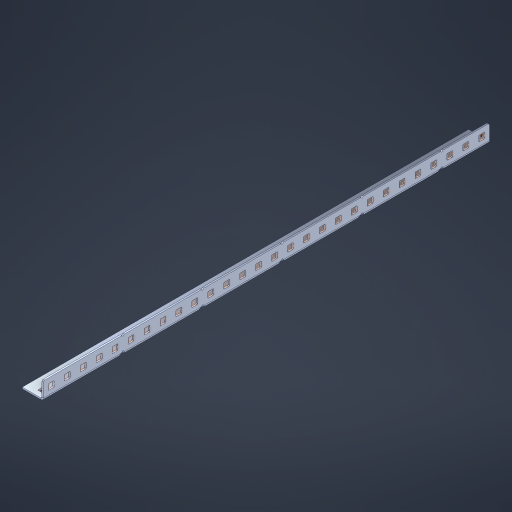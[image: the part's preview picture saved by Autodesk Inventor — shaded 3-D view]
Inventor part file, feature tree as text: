
AUTODESK INVENTOR PART (.ipt)
format: ipt  version: 2023 (Build 270158000, 158)  size: 908,288 bytes
history: native  units: in
note: dims shown in document units (in); Inventor stores cm internally (conversion verified against a paired STEP export)
features: other x61, extrude x55, sheet_metal_op x10, sketch x8, mirror x1, pattern_linear x1, chamfer x1
ambient origin geometry x8: Origin, YZ Plane, XZ Plane, XY Plane, X Axis, Y Axis, Z Axis, Center Point
bodies: Solid1 (feature_tree), Body (feature_tree)
feature tree (137):
  other  "Flange Pattern Plane"
  sheet_metal_op  "Flange Pattern"
  sheet_metal_op  "Body Pattern"
  other  "Arc Length"
  mirror  "Notch Mirror"
  pattern_linear  "Notch Pattern"  Spacing1=0.1875in  [1 undecoded]
  chamfer  "End Chamfer"
  extrude  "Half Cut"  Depth=0.0469in
  sketch  "Sketch1"  dims[d0=2.5in]
  other  "Plate1"
  sketch  "Sketch2"  dims[d1=14.0in]
  other  "Plate2"
  sheet_metal_op  "Bend1"
  sheet_metal_op  "Corner1"
  sketch  "Sketch3"  dims[d2=0.0469in]
  other  "Flange Pattern Sketch"
  sketch  "Sketch7"  dims[d3=0.0469in]
  other  "Srf1"
  other  "Srf2"
  sketch  "Sketch8"  dims[d4=0.0234in]
  sketch  "Sketch9"  dims[d5=0.0938in]
  other  "Srf91"
  sheet_metal_op  "Body Pattern Sketch"
  other  "Srf92"
  sketch  "Sketch13"  dims[d6=0.0469in]
  sketch  "Sketch14"  dims[d7=0.5in d8=90.0deg d9=0.0312in d10=0.1875in d11=0.0469in d12=0.0469in d16=0.182in d17=0.02in d18=0.0469in d19=0.0in d20=0.25in d21=0.25in d46=0.172in d47=1.0in d48=0.0in d49=0.182in d50=0.02in d51=0.25in d52=0.25in d53=0.0469in d54=0.0in d55=0.172in d56=1.0in d57=0.0in d60=11.0236in d62=0.5in d63=0.3937in d65=0.5in d85=0.1227in d86=0.1659in d88=0.04in d89=0.0469in d90=0.0in d91=0.04in d92=0.0491in d95=2.5in d96=0.04in d97=0.25in d98=45.0deg d101=0.0in d102=2.497in d131=0.5in d132=11.0236in d134=0.5in d139=0.5in]
  other  "Srf856"
  other  "Srf1310"
  other  "Srf1311"
  other  "Srf1312"
  other  "Srf1376"
  other  "Srf1377"
  other  "Srf1728"
  other  "Srf1755"
  other  "Srf1878"
  other  "Srf1879"
  other  "Srf1880"
  other  "Srf1881"
  other  "Srf1882"
  other  "Srf1883"
  other  "Srf1884"
  other  "Srf1885"
  other  "Srf1886"
  other  "Srf1887"
  other  "Srf1888"
  other  "Srf1889"
  other  "Srf1890"
  other  "Srf1891"
  other  "Srf1892"
  other  "Srf1893"
  other  "Srf1894"
  other  "Srf1895"
  other  "Srf1896"
  other  "Srf1897"
  other  "Srf1898"
  other  "Srf1899"
  other  "Srf1942"
  other  "Srf1943"
  other  "Srf1944"
  other  "Srf1945"
  other  "Srf1946"
  other  "Srf1947"
  other  "Srf1948"
  other  "Srf1949"
  other  "Srf1950"
  other  "Srf1951"
  other  "Srf1952"
  other  "Srf1953"
  other  "Srf1954"
  other  "Srf1955"
  other  "Srf1956"
  other  "Srf1957"
  other  "Srf1958"
  other  "Srf1959"
  other  "Srf1960"
  other  "Srf1961"
  other  "Srf1962"
  other  "Srf1963"
  sheet_metal_op  "Flange Stamp"
  sheet_metal_op  "Flange Circle"
  sheet_metal_op  "Body Stamp"
  sheet_metal_op  "Body Circle"
  sheet_metal_op  "Notch"
  extrude  "ExtrusionSrf2"  Depth=0.0469in
  extrude  "ExtrusionSrf92"  Depth=0.5in
  extrude  "ExtrusionSrf856"  Depth=0.02in
  extrude  "ExtrusionSrf1310"  Depth=0.0469in
  extrude  "ExtrusionSrf1311"  TaperAngle=0.0deg  [1 undecoded]
  extrude  "ExtrusionSrf1312"  Depth=0.5in
  extrude  "ExtrusionSrf1376"  Depth=0.5in
  extrude  "ExtrusionSrf1377"  Depth=0.5in
  extrude  "ExtrusionSrf1728"  Depth=0.5in TaperAngle=0.0deg
  extrude  "ExtrusionSrf1755"  Depth=0.5in
  extrude  "ExtrusionSrf1878"  Depth=0.02in
  extrude  "ExtrusionSrf1879"  Depth=0.5in
  extrude  "ExtrusionSrf1880"  Depth=0.5in
  extrude  "ExtrusionSrf1881"  Depth=0.0469in
  extrude  "ExtrusionSrf1882"  TaperAngle=0.0deg  [1 undecoded]
  extrude  "ExtrusionSrf1883"  Depth=0.5in
  extrude  "ExtrusionSrf1884"  Depth=0.5in TaperAngle=0.0deg
  extrude  "ExtrusionSrf1885"  Depth=0.5in
  extrude  "ExtrusionSrf1886"  Depth=0.5in
  extrude  "ExtrusionSrf1887"  Depth=0.5in
  extrude  "ExtrusionSrf1888"  Depth=0.5in
  extrude  "ExtrusionSrf1889"  Depth=0.5in
  extrude  "ExtrusionSrf1890"  Depth=0.0469in
  extrude  "ExtrusionSrf1891"  TaperAngle=0.0deg  [1 undecoded]
  extrude  "ExtrusionSrf1892"  Depth=0.5in
  extrude  "ExtrusionSrf1893"  Depth=0.5in
  extrude  "ExtrusionSrf1894"  Depth=0.5in
  extrude  "ExtrusionSrf1895"  Depth=0.5in TaperAngle=45.0deg
  extrude  "ExtrusionSrf1896"  TaperAngle=0.0deg  [1 undecoded]
  extrude  "ExtrusionSrf1897"  Depth=0.5in
  extrude  "ExtrusionSrf1898"  Depth=0.5in
  extrude  "ExtrusionSrf1899"  Depth=0.5in
  extrude  "ExtrusionSrf1942"  Depth=0.5in
  extrude  "ExtrusionSrf1943"  Depth=0.5in
  extrude  "ExtrusionSrf1944"  [1 undecoded]
  extrude  "ExtrusionSrf1945"  [1 undecoded]
  extrude  "ExtrusionSrf1946"  [1 undecoded]
  extrude  "ExtrusionSrf1947"  [1 undecoded]
  extrude  "ExtrusionSrf1948"  [1 undecoded]
  extrude  "ExtrusionSrf1949"  [1 undecoded]
  extrude  "ExtrusionSrf1950"  [1 undecoded]
  extrude  "ExtrusionSrf1951"  [1 undecoded]
  extrude  "ExtrusionSrf1952"  [1 undecoded]
  extrude  "ExtrusionSrf1953"  [1 undecoded]
  extrude  "ExtrusionSrf1954"  [1 undecoded]
  extrude  "ExtrusionSrf1955"  [1 undecoded]
  extrude  "ExtrusionSrf1956"  [1 undecoded]
  extrude  "ExtrusionSrf1957"  [1 undecoded]
  extrude  "ExtrusionSrf1958"  [1 undecoded]
  extrude  "ExtrusionSrf1959"  [1 undecoded]
  extrude  "ExtrusionSrf1960"  [1 undecoded]
  extrude  "ExtrusionSrf1961"  [1 undecoded]
  extrude  "ExtrusionSrf1962"  [1 undecoded]
  extrude  "ExtrusionSrf1963"  [1 undecoded]
note: 25 required parameter values undecoded (feature->parameter linkage not recoverable at this tier; creation-order binding heuristic only, values carry confidence <= 0.55)
